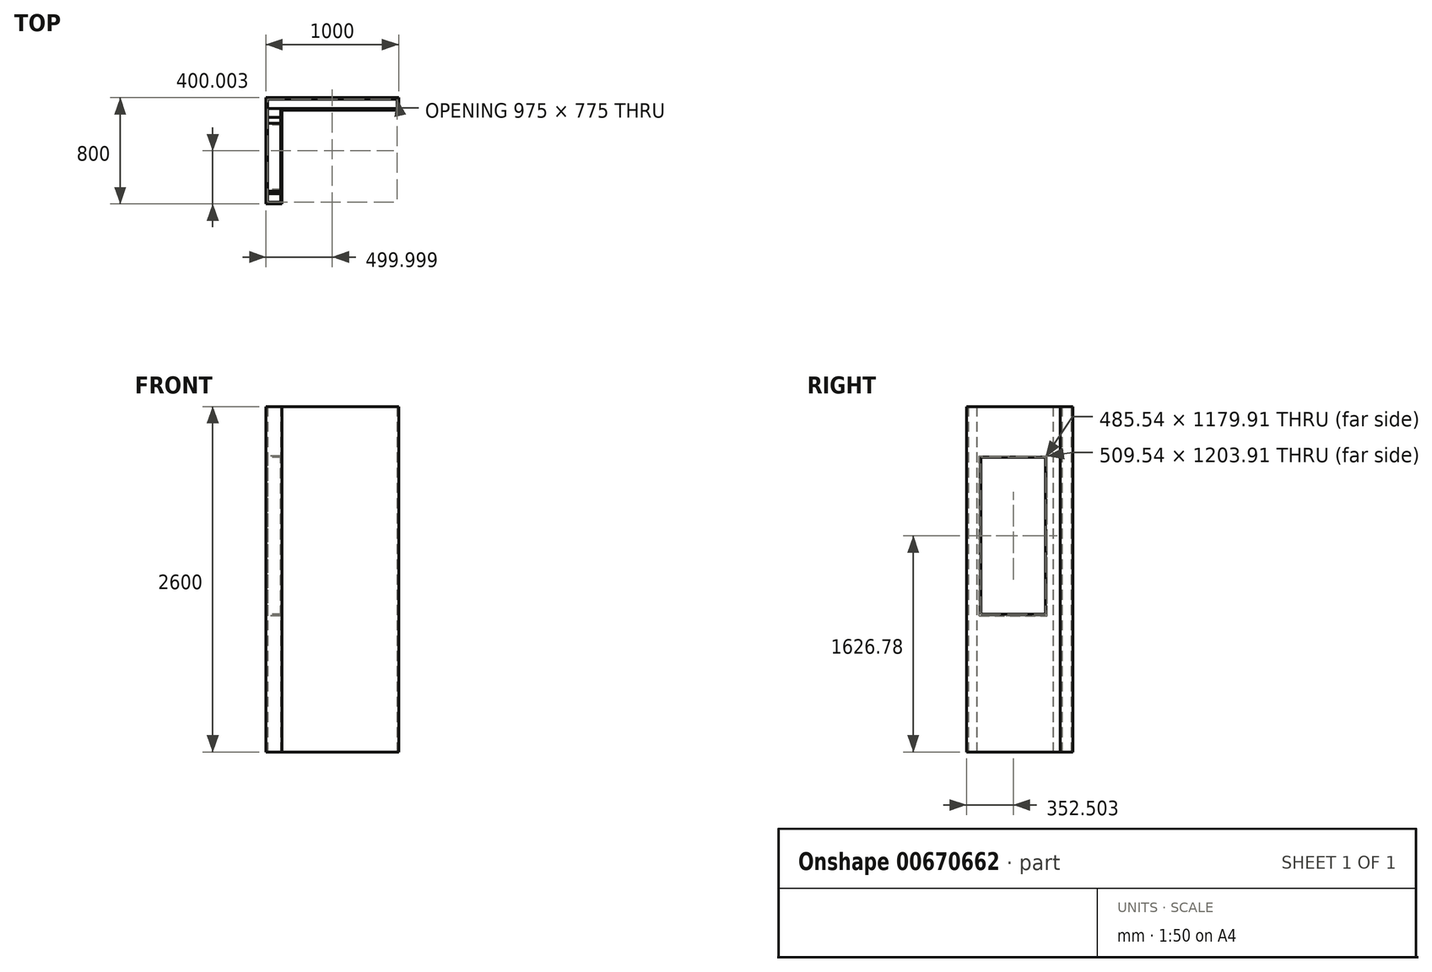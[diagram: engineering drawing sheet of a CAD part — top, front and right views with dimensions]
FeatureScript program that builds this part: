
annotation { "Feature Type Name" : "Feature", "Feature Type Description" : "" }
export const myFeature = defineFeature(function(context is Context, id is Id, definition is map)
    precondition{}
    {
        {
            var Q0;
            Q0=qCreatedBy(makeId("Top.planeOp"),FACE);
            var sketch = newSketch(context, id + "F0", { "sketchPlane" : qUnion([Q0])});
            skLineSegment(sketch, "E0", {"start": v(-1175.1, 302.92) * mm, "end": v(-1175.1, 1007.92) * mm});
            skLineSegment(sketch, "E1", {"start": v(-1175.1, 1007.92) * mm, "end": v(-297.6, 1007.92) * mm});
            skLineSegment(sketch, "E2", {"start": v(-297.6, 1007.92) * mm, "end": v(-297.6, 1102.92) * mm});
            skLineSegment(sketch, "E3", {"start": v(-297.6, 1102.92) * mm, "end": v(-1297.6, 1102.92) * mm});
            skLineSegment(sketch, "E4", {"start": v(-1297.6, 1102.92) * mm, "end": v(-1297.6, 302.92) * mm});
            skLineSegment(sketch, "E5", {"start": v(-1297.6, 302.92) * mm, "end": v(-1175.1, 302.92) * mm});
            skLineSegment(sketch, "E6.0", {"start": v(-1187.6, 1020.42) * mm, "end": v(-310.1, 1020.42) * mm});
            skLineSegment(sketch, "E6.1", {"start": v(-310.1, 1090.42) * mm, "end": v(-1285.1, 1090.42) * mm});
            skLineSegment(sketch, "E6.2", {"start": v(-1285.1, 1090.42) * mm, "end": v(-1285.1, 315.42) * mm});
            skLineSegment(sketch, "E6.3", {"start": v(-310.1, 1020.42) * mm, "end": v(-310.1, 1090.42) * mm});
            skLineSegment(sketch, "E6.4", {"start": v(-1285.1, 315.42) * mm, "end": v(-1187.6, 315.42) * mm});
            skLineSegment(sketch, "E6.5", {"start": v(-1187.6, 315.42) * mm, "end": v(-1187.6, 1020.42) * mm});
            skLineSegment(sketch, "E7.top", {"start": v(-1285.1, 381.07) * mm, "end": v(-1187.6, 381.07) * mm});
            skLineSegment(sketch, "E7.left", {"start": v(-1285.1, 315.42) * mm, "end": v(-1285.1, 381.07) * mm});
            skLineSegment(sketch, "E7.right", {"start": v(-1187.6, 315.42) * mm, "end": v(-1187.6, 381.07) * mm});
            skLineSegment(sketch, "E8", {"start": v(-1187.6, 667.92) * mm, "end": v(-1285.1, 667.92) * mm, "construction": true});
            skPoint(sketch, "E8.endSnap0", {"position": v(-1285.1, 702.92) * mm});
            skLineSegment(sketch, "E9.MirrorCS", {"start": v(-1285.1, 954.78) * mm, "end": v(-1187.6, 954.78) * mm});
            skLineSegment(sketch, "E10.MirrorCS", {"start": v(-1285.1, 1020.42) * mm, "end": v(-1187.6, 1020.42) * mm});
            skLineSegment(sketch, "E11.bottom", {"start": v(-1187.6, 1020.42) * mm, "end": v(-1118.88, 1020.42) * mm});
            skLineSegment(sketch, "E11.top", {"start": v(-1187.6, 1090.42) * mm, "end": v(-1118.88, 1090.42) * mm});
            skLineSegment(sketch, "E11.left", {"start": v(-1187.6, 1020.42) * mm, "end": v(-1187.6, 1090.42) * mm});
            skLineSegment(sketch, "E11.right", {"start": v(-1118.88, 1020.42) * mm, "end": v(-1118.88, 1090.42) * mm});
            skLineSegment(sketch, "E12.bottom", {"start": v(-310.1, 1020.42) * mm, "end": v(-378.86, 1020.42) * mm});
            skLineSegment(sketch, "E12.top", {"start": v(-310.1, 1090.42) * mm, "end": v(-378.86, 1090.42) * mm});
            skLineSegment(sketch, "E12.right", {"start": v(-378.86, 1020.42) * mm, "end": v(-378.86, 1090.42) * mm});
            skSolve(sketch);
        }
        {
            var Q0;
            Q0=makeQuery(id+"F0.imprint","IMPRINT",FACE,{"disambiguationData":[TD([[makeQuery(id+"F0.imprint","IMPRINT",EDGE,{"derivedFrom":sQuery(id+"F0.wireOp",EDGE,"E0")}),1.0]])]});
            extrude(context, id + "F1", {"entities" : qUnion([Q0]), "depth" : 2600 * mm, "offsetDistance" : 25 * mm});
        }
        {
            var Q0;
            Q0=makeQuery(id+"F0.imprint","IMPRINT",FACE,{"disambiguationData":[TD([[makeQuery(id+"F0.imprint","IMPRINT",EDGE,{"derivedFrom":sQuery(id+"F0.wireOp",EDGE,"E6.4")}),1.0]])]});
            var Q1;
            {var subQ0=sQuery(id+"F0.wireOp",EDGE,"E9.MirrorCS");Q1=makeQuery(id+"F0.imprint","IMPRINT",FACE,{"disambiguationData":[TD([[makeQuery(id+"F0.imprint","IMPRINT",EDGE,{"derivedFrom":subQ0}),1.0]])]});}
            var Q2;
            Q2=makeQuery(id+"F0.imprint","IMPRINT",FACE,{"disambiguationData":[TD([[makeQuery(id+"F0.imprint","IMPRINT",EDGE,{"derivedFrom":sQuery(id+"F0.wireOp",EDGE,"E11.bottom")}),1.0]])]});
            var Q3;
            Q3=makeQuery(id+"F0.imprint","IMPRINT",FACE,{"disambiguationData":[TD([[makeQuery(id+"F0.imprint","IMPRINT",EDGE,{"derivedFrom":sQuery(id+"F0.wireOp",EDGE,"E12.bottom")}),-1.0]])]});
            extrude(context, id + "F2", {"entities" : qUnion([Q0, Q1, Q2, Q3]), "depth" : 2600 * mm, "offsetDistance" : 25 * mm});
        }
        {
            var Q0;
            Q0=makeQuery(id+"F1.opExtrude","SWEPT_FACE",FACE,{"disambiguationData":[OSD([sQuery(id+"F0.wireOp",EDGE,"E0")])]});
            var sketch = newSketch(context, id + "F3", { "sketchPlane" : qUnion([Q0])});
            skLineSegment(sketch, "E13", {"start": v(655.42, 0) * mm, "end": v(655.42, 2600) * mm, "construction": true});
            skLineSegment(sketch, "E14.bottom", {"start": v(910.2, 2228.73) * mm, "end": v(400.65, 2228.73) * mm});
            skLineSegment(sketch, "E14.top", {"start": v(910.2, 1024.82) * mm, "end": v(400.65, 1024.82) * mm});
            skLineSegment(sketch, "E14.left", {"start": v(910.2, 2228.73) * mm, "end": v(910.2, 1024.82) * mm});
            skLineSegment(sketch, "E14.right", {"start": v(400.65, 2228.73) * mm, "end": v(400.65, 1024.82) * mm});
            skPoint(sketch, "E14.middle", {"position": v(655.42, 1626.77) * mm});
            skSolve(sketch);
        }
        {
            var Q0;
            Q0=makeQuery(id+"F3.imprint","IMPRINT",FACE,{"disambiguationData":[TD([[makeQuery(id+"F3.imprint","IMPRINT",EDGE,{"derivedFrom":sQuery(id+"F3.wireOp",EDGE,"E14.bottom")}),1.0]])]});
            extrude(context, id + "F4", {"entities" : qUnion([Q0]), "operationType" : NewBodyOperationType.REMOVE, "endBound" : BoundingType.THROUGH_ALL, "oppositeDirection" : true, "depth" : 25 * mm, "offsetDistance" : 25 * mm});
        }
        {
            var Q0;
            Q0=makeQuery(id+"F1.opExtrude","SWEPT_FACE",FACE,{"disambiguationData":[OSD([sQuery(id+"F0.wireOp",EDGE,"E4")])]});
            var sketch = newSketch(context, id + "F5", { "sketchPlane" : qUnion([Q0])});
            skLineSegment(sketch, "E15.0", {"start": v(-898.2, 2216.73) * mm, "end": v(-412.65, 2216.73) * mm});
            skLineSegment(sketch, "E15.1", {"start": v(-898.2, 2216.73) * mm, "end": v(-898.2, 1036.82) * mm});
            skLineSegment(sketch, "E15.2", {"start": v(-898.2, 1036.82) * mm, "end": v(-412.65, 1036.82) * mm});
            skLineSegment(sketch, "E15.3", {"start": v(-412.65, 2216.73) * mm, "end": v(-412.65, 1036.82) * mm});
            skSolve(sketch);
        }
        {
            var Q0;
            Q0=makeQuery(id+"F5.imprint","IMPRINT",FACE,{"disambiguationData":[TD([[makeQuery(id+"F5.imprint","IMPRINT",EDGE,{"derivedFrom":sQuery(id+"F5.wireOp",EDGE,"E15.0")}),1.0]])]});
            var Q1;
            Q1=makeQuery(id+"F1.opExtrude","SWEPT_FACE",FACE,{"disambiguationData":[OSD([sQuery(id+"F0.wireOp",EDGE,"E0")])]});
            extrude(context, id + "F6", {"entities" : qUnion([Q0]), "operationType" : NewBodyOperationType.ADD, "endBound" : BoundingType.UP_TO_SURFACE, "oppositeDirection" : true, "depth" : 25 * mm, "endBoundEntityFace" : qUnion([Q1]), "offsetDistance" : 25 * mm});
        }
    });
